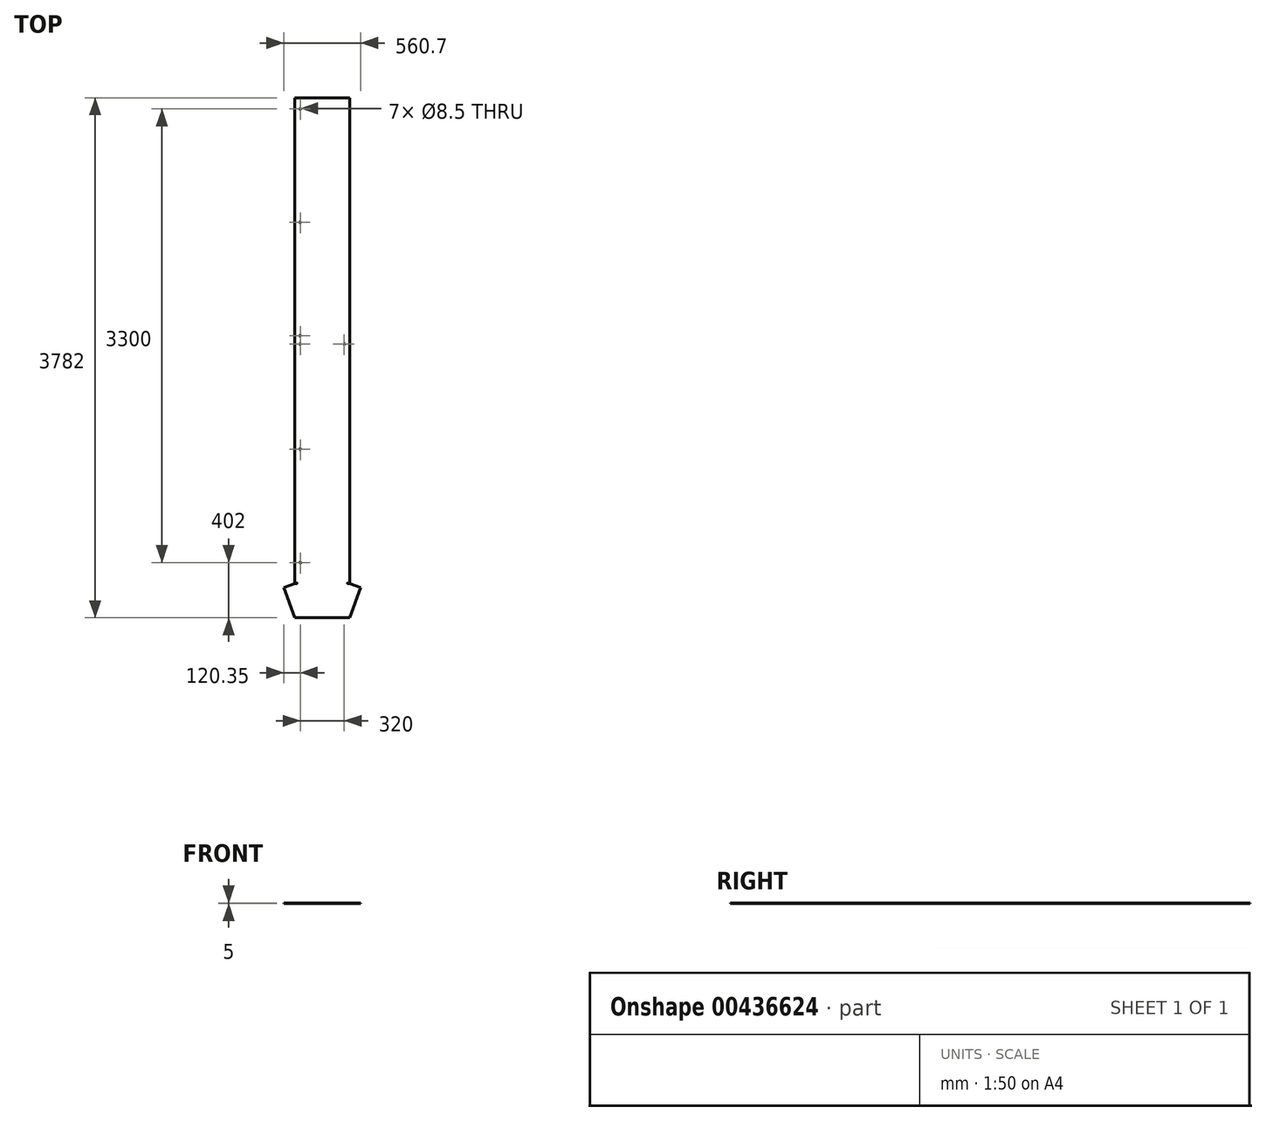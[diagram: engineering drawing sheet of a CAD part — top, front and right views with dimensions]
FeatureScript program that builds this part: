
annotation { "Feature Type Name" : "Feature", "Feature Type Description" : "" }
export const myFeature = defineFeature(function(context is Context, id is Id, definition is map)
    precondition{}
    {
        {
            var Q0;
            Q0=qCreatedBy(makeId("Top.planeOp"),FACE);
            var sketch = newSketch(context, id + "F0", { "sketchPlane" : qUnion([Q0])});
            skLineSegment(sketch, "E0.bottom", {"start": v(200, 1765) * mm, "end": v(-200, 1765) * mm});
            skLineSegment(sketch, "E0.top", {"start": v(-183, -1765) * mm, "end": v(-200, -1765) * mm});
            skLineSegment(sketch, "E0.left", {"start": v(200, 1765) * mm, "end": v(200, -1765) * mm});
            skLineSegment(sketch, "E0.right", {"start": v(-200, 1765) * mm, "end": v(-200, -1765) * mm});
            skPoint(sketch, "E0.middle", {"position": v(0, 0) * mm});
            skLineSegment(sketch, "E1", {"start": v(-182.5, -1765.5) * mm, "end": v(-182.5, -1766.5) * mm});
            skLineSegment(sketch, "E2", {"start": v(-183, -1767) * mm, "end": v(-200, -1767) * mm});
            skLineSegment(sketch, "E3", {"start": v(-200, -1767) * mm, "end": v(-280.35, -1796.24) * mm});
            skLineSegment(sketch, "E4", {"start": v(-280.35, -1796.24) * mm, "end": v(-200, -2017) * mm});
            skLineSegment(sketch, "E5", {"start": v(-200, -2017) * mm, "end": v(200, -2017) * mm});
            skPoint(sketch, "E6.visualSharp", {"position": v(-182.5, -1765) * mm});
            skArc(sketch, "E6.filletArc", {"start": v(-182.5, -1765.5) * mm, "mid": v(-182.65, -1765.15) * mm, "end": v(-183, -1765) * mm});
            skPoint(sketch, "E7.visualSharp", {"position": v(-182.5, -1767) * mm});
            skArc(sketch, "E7.filletArc", {"start": v(-183, -1767) * mm, "mid": v(-182.65, -1766.85) * mm, "end": v(-182.5, -1766.5) * mm});
            skLineSegment(sketch, "E8", {"start": v(0, -2017) * mm, "end": v(0, 0) * mm, "construction": true});
            skLineSegment(sketch, "E9.MirrorCS", {"start": v(183, -1765) * mm, "end": v(200, -1765) * mm});
            skArc(sketch, "E10.MirrorCS", {"start": v(182.5, -1765.5) * mm, "mid": v(182.65, -1765.15) * mm, "end": v(183, -1765) * mm});
            skLineSegment(sketch, "E11.MirrorCS", {"start": v(182.5, -1765.5) * mm, "end": v(182.5, -1766.5) * mm});
            skPoint(sketch, "E12.MirrorP", {"position": v(182.5, -1767) * mm});
            skArc(sketch, "E13.MirrorCS", {"start": v(183, -1767) * mm, "mid": v(182.65, -1766.85) * mm, "end": v(182.5, -1766.5) * mm});
            skLineSegment(sketch, "E14.MirrorCS", {"start": v(183, -1767) * mm, "end": v(200, -1767) * mm});
            skLineSegment(sketch, "E15.MirrorCS", {"start": v(200, -1767) * mm, "end": v(280.35, -1796.24) * mm});
            skLineSegment(sketch, "E16.MirrorCS", {"start": v(280.35, -1796.24) * mm, "end": v(200, -2017) * mm});
            skSolve(sketch);
        }
        {
            var Q0;
            Q0 = qSketchRegion(id + "F0", true);
            extrude(context, id + "F1", {"entities" : qUnion([Q0]), "depth" : 5 * mm});
        }
        {
            var Q0;
            Q0=makeQuery(id+"F1.opExtrude","CAP_FACE",FACE,{"disambiguationData":[OSD([sQuery(id+"F0.wireOp",EDGE,"E0.bottom"),sQuery(id+"F0.wireOp",EDGE,"E0.top"),sQuery(id+"F0.wireOp",EDGE,"E0.left"),sQuery(id+"F0.wireOp",EDGE,"E0.right"),sQuery(id+"F0.wireOp",EDGE,"E1"),sQuery(id+"F0.wireOp",EDGE,"E2"),sQuery(id+"F0.wireOp",EDGE,"E3"),sQuery(id+"F0.wireOp",EDGE,"E4"),sQuery(id+"F0.wireOp",EDGE,"E5"),sQuery(id+"F0.wireOp",EDGE,"E6.filletArc"),sQuery(id+"F0.wireOp",EDGE,"E7.filletArc"),sQuery(id+"F0.wireOp",EDGE,"E9.MirrorCS"),sQuery(id+"F0.wireOp",EDGE,"E10.MirrorCS"),sQuery(id+"F0.wireOp",EDGE,"E11.MirrorCS"),sQuery(id+"F0.wireOp",EDGE,"E13.MirrorCS"),sQuery(id+"F0.wireOp",EDGE,"E14.MirrorCS"),sQuery(id+"F0.wireOp",EDGE,"E15.MirrorCS"),sQuery(id+"F0.wireOp",EDGE,"E16.MirrorCS")])],"isStart":false});
            var sketch = newSketch(context, id + "F2", { "sketchPlane" : qUnion([Q0])});
            skLineSegment(sketch, "E17", {"start": v(0, 1765) * mm, "end": v(0, 1338.14) * mm, "construction": true});
            skPoint(sketch, "E17.endSnap0", {"position": v(0, 1765) * mm});
            skCircle(sketch, "E18", {"center": v(-160, 1685) * mm, "radius": 4.25 * mm});
            skCircle(sketch, "E19.0.1.0", {"center": v(-160, 860) * mm, "radius": 4.25 * mm});
            skCircle(sketch, "E19.0.2.0", {"center": v(-160, 35) * mm, "radius": 4.25 * mm});
            skCircle(sketch, "E19.0.3.0", {"center": v(-160, -790) * mm, "radius": 4.25 * mm});
            skCircle(sketch, "E19.0.4.0", {"center": v(-160, -1615) * mm, "radius": 4.25 * mm});
            skLineSegment(sketch, "E19.direction1", {"start": v(-160, 1685) * mm, "end": v(-135, 1685) * mm, "construction": true});
            skLineSegment(sketch, "E19.direction2", {"start": v(-160, 1685) * mm, "end": v(-160, 860) * mm, "construction": true});
            skSolve(sketch);
        }
        {
            var Q0;
            Q0 = qSketchRegion(id + "F2", true);
            extrude(context, id + "F3", {"entities" : qUnion([Q0]), "operationType" : NewBodyOperationType.REMOVE, "endBound" : BoundingType.THROUGH_ALL, "oppositeDirection" : true, "depth" : 25 * mm});
        }
        {
            var Q0;
            Q0=makeQuery(id+"F1.opExtrude","CAP_FACE",FACE,{"disambiguationData":[OSD([sQuery(id+"F0.wireOp",EDGE,"E0.bottom"),sQuery(id+"F0.wireOp",EDGE,"E0.top"),sQuery(id+"F0.wireOp",EDGE,"E0.left"),sQuery(id+"F0.wireOp",EDGE,"E0.right"),sQuery(id+"F0.wireOp",EDGE,"E1"),sQuery(id+"F0.wireOp",EDGE,"E2"),sQuery(id+"F0.wireOp",EDGE,"E3"),sQuery(id+"F0.wireOp",EDGE,"E4"),sQuery(id+"F0.wireOp",EDGE,"E5"),sQuery(id+"F0.wireOp",EDGE,"E6.filletArc"),sQuery(id+"F0.wireOp",EDGE,"E7.filletArc"),sQuery(id+"F0.wireOp",EDGE,"E9.MirrorCS"),sQuery(id+"F0.wireOp",EDGE,"E10.MirrorCS"),sQuery(id+"F0.wireOp",EDGE,"E11.MirrorCS"),sQuery(id+"F0.wireOp",EDGE,"E13.MirrorCS"),sQuery(id+"F0.wireOp",EDGE,"E14.MirrorCS"),sQuery(id+"F0.wireOp",EDGE,"E15.MirrorCS"),sQuery(id+"F0.wireOp",EDGE,"E16.MirrorCS")])],"isStart":false});
            var sketch = newSketch(context, id + "F4", { "sketchPlane" : qUnion([Q0])});
            skCircle(sketch, "E20", {"center": v(-160, -25) * mm, "radius": 4.25 * mm});
            skPoint(sketch, "E21", {"position": v(-160, 35) * mm});
            skLineSegment(sketch, "E22", {"start": v(0, 0) * mm, "end": v(0, 110.4) * mm, "construction": true});
            skCircle(sketch, "E23.MirrorC", {"center": v(160, -25) * mm, "radius": 4.25 * mm});
            skSolve(sketch);
        }
        {
            var Q0;
            Q0 = qSketchRegion(id + "F4", true);
            extrude(context, id + "F5", {"entities" : qUnion([Q0]), "operationType" : NewBodyOperationType.REMOVE, "endBound" : BoundingType.THROUGH_ALL, "oppositeDirection" : true, "depth" : 25 * mm});
        }
    });
